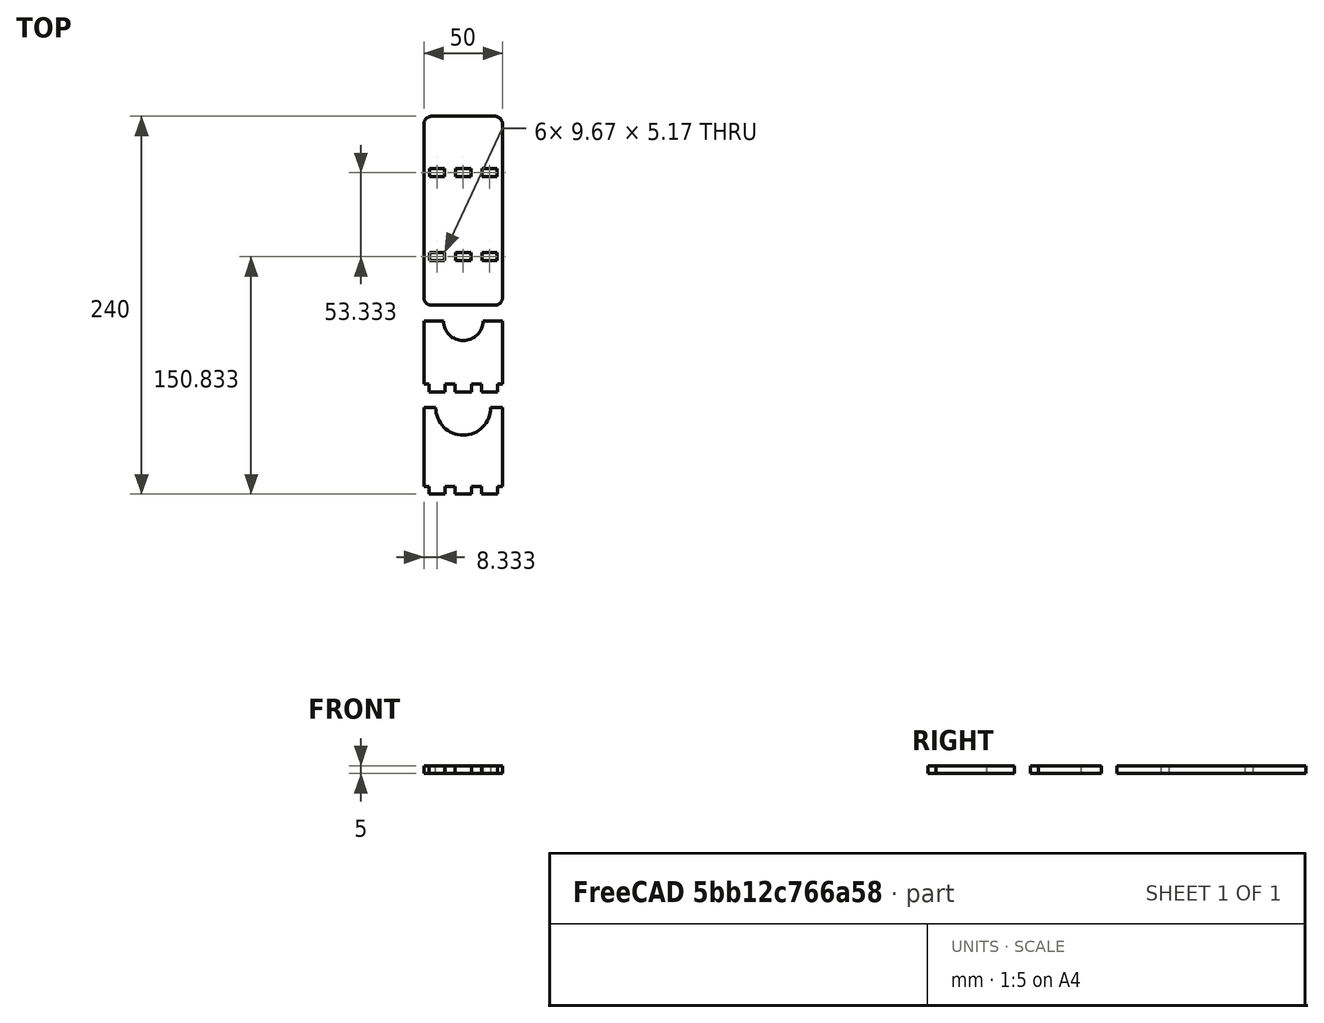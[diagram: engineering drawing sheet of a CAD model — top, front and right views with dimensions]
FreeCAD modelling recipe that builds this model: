
FCSTD DOCUMENT  (FreeCAD 0.19R24276 (Git))
Label: exported_parts
License: All rights reserved
LicenseURL: http://en.wikipedia.org/wiki/All_rights_reserved
objects: Part::Feature×3, Part::Part2DObjectPython×3
note: 6 computed .brp shape members not serialized (recipe doc carries the construction recipe); baked Part::Feature solids carry a one-line shape summary decoded from their .brp

FEATURE [Part::Feature] test
  Placement = pos=(25,30,56.6667) rot=(-1,0,0;1.5708rad)
  shape: bbox 50 x 55 x 5 mm, 20 faces (baked)
FEATURE [Part::Feature] test001
  Placement = pos=(25,95,3.33333) rot=(-1,0,0;1.5708rad)
  shape: bbox 50 x 45 x 5 mm, 20 faces (baked)
FEATURE [Part::Feature] test002
  Placement = pos=(25,180,5) rot=(0,-1,0;3.14159rad)
  shape: bbox 50 x 120 x 5 mm, 34 faces (baked)
FEATURE [Part::Part2DObjectPython] Shape2DView  # Draft 2D object (typed FeaturePython)
  Base = -> test
  FuseArch = false
  HiddenLines = false
  InPlace = true
  Projection = (0,0,1)
  ProjectionMode = 0
  SegmentLength = 0.05
  Tessellation = false
  VisibleOnly = false
FEATURE [Part::Part2DObjectPython] Shape2DView001  # Draft 2D object (typed FeaturePython)
  Base = -> test001
  FuseArch = false
  HiddenLines = false
  InPlace = true
  Projection = (0,0,1)
  ProjectionMode = 0
  SegmentLength = 0.05
  Tessellation = false
  VisibleOnly = false
FEATURE [Part::Part2DObjectPython] Shape2DView002  # Draft 2D object (typed FeaturePython)
  Base = -> test002
  FuseArch = false
  HiddenLines = false
  InPlace = true
  Projection = (0,0,1)
  ProjectionMode = 0
  SegmentLength = 0.05
  Tessellation = false
  VisibleOnly = false
